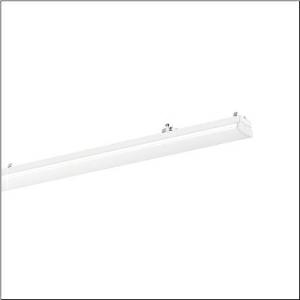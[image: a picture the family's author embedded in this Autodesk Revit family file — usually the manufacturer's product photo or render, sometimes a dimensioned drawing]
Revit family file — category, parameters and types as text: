
# Revit family: licross_r__11_recessed_opal_ho_51tl1ddn46xm_4fcf
name_source: partatom
category: Lighting Fixtures
units: mm (PartAtom-declared; Revit-internal decimal feet)

## family parameters
Cut with Voids When Loaded = No
Host = Face
Light Source = No
Part Type = Normal
Room Calculation Point = No
Round Connector Dimension = Use Diameter
Shared = No

## types (1)
- --- (1 x LED, 6320 lm, 33.5 W, 4000K)
    Apparent Load = 34 VA
    CIE Flux Codes = 44 73 91 87 100
    Color Rendering = 80
    Color Temperature = 4000K
    Default Elevation = 1800 mm
    Description = Licross® 11 recessed opal HO, luminaire insert, of sheet steel, coil coated, white, length: 1.500mm, width: 76mm, height: 87mm, LED rated luminous flux: 6.320lm, light colour: 840, control gear: DALI 2, with plug, 5-pole, with phase selection, mains connection: 220..240V, AC, 50/60Hz, rated input power: 34W, halogen-free wiring, primary optical cover: cover, of PMMA, light emission: direct with ceiling illumination distribution, primary light characteristic: symmetric, protection rating (complete): IP40, insulation class (complete): insulation class I (protective earthing), certification: CE, ENEC, VDE, UKCA, protection symbol: D if used in an environment without relevant dust loads with corresponding accessories, impact resistance: IK06, permissible ambient temperature for indoor applications: -25..+45°C, corresponds to IFS (International Featured Standards) requirements for safety and quality in the food industry, reducing of maximum allowable ambient temperature of 5°C with ceiling mounting, LABS conformity tested according to VDMA 24364:2018-05, packaging unit: 1 piece
    Height = 83 mm
    Lamp = 1 x LED
    Lamp Light Flux = 6320 lm
    Lamp Power = 33.5 W
    Lamp count = 1
    Length = 1500 mm
    Luminous efficacy = 189 lm/W
    Manufacturer = Siteco
    ModVariant = No
    Model = 51TL1DDN46XM
    Mounting Place = Ceiling
    Mounting Type = Pendant
    Number of Poles = 1
    OnlyDefault = Yes
    Power Factor = 1
    Product Name = Licross® 11 recessed opal HO
    Product group = luminaire insert
    ProductGroupID = 902
    Protection Class = Protection class I
    Protection Degree = IP 40
    RLX_Detail_Level = 1
    RLX_Emergency_Light_Flux = 0 lm
    RLX_Emergency_Type = 0
    RLX_Emergency_Type_DB = No
    RlxData = <blob elided: 26689 chars, md5=3966d2a7>
    Socket = socket
    Standby Power = 0 W
    System Light Flux = 6320 lm
    System Power = 34 W
    Type Comments = factory setting: luminous flux: 100 % | dim-lin: 254 | 232 mA
    Type Image = l_1313666.jpg
    URL = http://relux.com
    VarID = @adj_076108
    Voltage = 0 V
    Weight = 0.00 kg
    Width = 76 mm

## geometry (parser evidence)
native form markers: Blend x4, Sweep x13
no freeform markers — native parametric forms only
